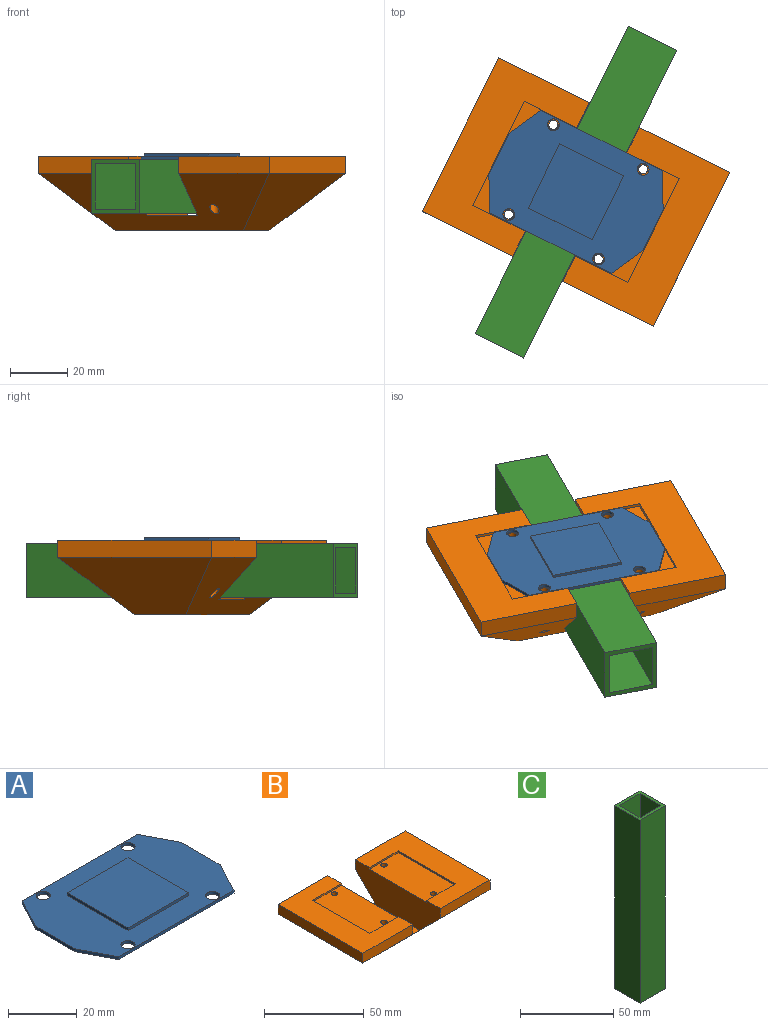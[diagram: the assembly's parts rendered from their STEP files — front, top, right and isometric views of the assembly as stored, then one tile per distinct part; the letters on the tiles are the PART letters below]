
ASSEMBLY  parts=3 mates=6
PART A: 19 faces, bbox 60x40x2 mm
  f0: plane 60x40mm, normal (0,0,1), area 1572.2mm2, adj f1,f2,f3,f4,f6,f7,f8,f9
  f1: plane 16x1mm, normal (1,0,0), area 16mm2, adj f0,f5,f12,f13
  f2: plane 47.5x1mm, normal (0,1,0), area 47.5mm2, adj f0,f5,f10,f13
  f3: plane 16x1mm, normal (-1,0,0), area 16mm2, adj f0,f5,f10,f11
  f4: plane 47.5x1mm, normal (0,-1,0), area 47.5mm2, adj f0,f5,f11,f12
  f5: plane 60x40mm, normal (0,0,-1), area 2197.2mm2, adj f1,f2,f3,f4,f6,f7,f8,f9
  f6: cylinder r=2.05mm len=4.1mm, axis (0,0,-1), area 12.9mm2, adj f0,f5
  f7: cylinder r=2.05mm len=4.1mm, axis (0,0,-1), area 12.9mm2, adj f0,f5
  f8: cylinder r=2.05mm len=4.1mm, axis (0,0,-1), area 12.9mm2, adj f0,f5
  f9: cylinder r=2.05mm len=4.1mm, axis (0,0,-1), area 12.9mm2, adj f0,f5
  f10: plane 12x6.25mm, normal (-0.89,0.46,0), area 13.5mm2, adj f0,f2,f3,f5
  f11: plane 12x6.25mm, normal (-0.89,-0.46,0), area 13.5mm2, adj f0,f3,f4,f5
  f12: plane 12x6.25mm, normal (0.89,-0.46,0), area 13.5mm2, adj f0,f1,f4,f5
  f13: plane 12x6.25mm, normal (0.89,0.46,0), area 13.5mm2, adj f0,f1,f2,f5
  f14: plane 25x1mm, normal (0,-1,0), area 25mm2, adj f0,f15,f17,f18
  f15: plane 25x1mm, normal (1,0,0), area 25mm2, adj f0,f14,f16,f18
  f16: plane 25x1mm, normal (0,1,0), area 25mm2, adj f0,f15,f17,f18
  f17: plane 25x1mm, normal (-1,0,0), area 25mm2, adj f0,f14,f16,f18
  f18: plane 25x25mm, normal (0,0,1), area 625mm2, adj f14,f15,f16,f17
PART B: 28 faces, bbox 90.7x60.7x26.7 mm
  f0: plane 35.23x6mm, normal (0,-1,0), area 211.4mm2, adj f7,f10,f12,f21
  f1: plane 35.23x6mm, normal (0,1,0), area 211.4mm2, adj f6,f9,f16,f22
  f2: plane 40.5x20.48mm, normal (0,0,1), area 813.2mm2, adj f10,f13,f14,f15,f24,f27
  f3: plane 40.5x20.48mm, normal (0,0,1), area 813.2mm2, adj f9,f17,f18,f19,f25,f26
  f4: plane 35.23x6mm, normal (0,-1,0), area 211.4mm2, adj f6,f9,f16,f21
  f5: plane 35.23x6mm, normal (0,1,0), area 211.4mm2, adj f7,f10,f12,f22
  f6: plane 60x6mm, normal (1,0,0), area 360mm2, adj f1,f4,f16,f20
  f7: plane 60x6mm, normal (-1,0,0), area 360mm2, adj f0,f5,f12,f23
  f8: plane 50x20mm, normal (0,0,-1), area 1000mm2, adj f20,f21,f22,f23
  f9: plane 60x20.55mm, normal (-1,0,0), area 980.8mm2, adj f1,f3,f4,f11,f16,f17,f18,f21
  f10: plane 60x20.55mm, normal (1,0,0), area 980.8mm2, adj f0,f2,f5,f11,f12,f13,f15,f21
  f11: plane 30.9x19.55mm, normal (0,0,1), area 604.1mm2, adj f9,f10,f21,f22
  f12: plane 60x35.23mm, normal (0,0,1), area 1284.3mm2, adj f0,f5,f7,f10,f13,f14,f15
  f13: plane 20.48x1mm, normal (0,1,0), area 20.5mm2, adj f2,f10,f12,f14
  f14: plane 40.5x1mm, normal (1,0,0), area 40.5mm2, adj f2,f12,f13,f15
  f15: plane 20.48x1mm, normal (0,-1,0), area 20.5mm2, adj f2,f10,f12,f14
  f16: plane 60x35.23mm, normal (0,0,1), area 1284.3mm2, adj f1,f4,f6,f9,f17,f18,f19
  f17: plane 20.48x1mm, normal (0,1,0), area 20.5mm2, adj f3,f9,f16,f19
  f18: plane 20.48x1mm, normal (0,-1,0), area 20.5mm2, adj f3,f9,f16,f19
  f19: plane 40.5x1mm, normal (-1,0,0), area 40.5mm2, adj f3,f16,f17,f18
  f20: plane 60x20mm, normal (0.71,0,-0.71), area 1131.4mm2, adj f6,f8,f21,f22
  f21: plane 90.67x20.67mm, normal (0,-0.71,-0.71), area 1554.9mm2, adj f0,f4,f8,f9,f10,f11,f20,f23
  f22: plane 90.67x20.67mm, normal (0,0.71,-0.71), area 1554.9mm2, adj f1,f5,f8,f9,f10,f11,f20,f23
  f23: plane 60x20mm, normal (-0.71,0,-0.71), area 1131.4mm2, adj f7,f8,f21,f22
  f24: cylinder r=1.6mm len=19.11mm, axis (0,0,1), area 176.5mm2, adj f2,f22
  f25: cylinder r=1.6mm len=19.11mm, axis (0,0,1), area 176.5mm2, adj f3,f22
  f26: cylinder r=1.6mm len=19.11mm, axis (0,0,1), area 176.5mm2, adj f3,f21
  f27: cylinder r=1.6mm len=19.11mm, axis (0,0,1), area 176.5mm2, adj f2,f21
PART C: 10 faces, bbox 19.1x19.1x120 mm
  f0: plane 120x19.05mm, normal (0,-1,0), area 2286mm2, adj f1,f7,f8,f9
  f1: plane 120x19.05mm, normal (1,0,0), area 2286mm2, adj f0,f2,f8,f9
  f2: plane 120x19.05mm, normal (0,1,0), area 2286mm2, adj f1,f7,f8,f9
  f3: plane 120x15.88mm, normal (0,-1,0), area 1905mm2, adj f4,f6,f8,f9
  f4: plane 120x15.88mm, normal (-1,0,0), area 1905mm2, adj f3,f5,f8,f9
  f5: plane 120x15.88mm, normal (0,1,0), area 1905mm2, adj f4,f6,f8,f9
  f6: plane 120x15.88mm, normal (1,0,0), area 1905mm2, adj f3,f5,f8,f9
  f7: plane 120x19.05mm, normal (-1,0,0), area 2286mm2, adj f0,f2,f8,f9
  f8: plane 19.05x19.05mm, normal (0,0,1), area 110.9mm2, adj f0,f1,f2,f3,f4,f5,f6,f7
  f9: plane 19.05x19.05mm, normal (0,0,-1), area 110.9mm2, adj f0,f1,f2,f3,f4,f5,f6,f7
PLACE A rot(axis=(0,0,1),153.6deg) t=(0,0,-1)mm
PLACE B rot(axis=(0,0,-1),26.4deg) t=(0,0,-1)mm
PLACE C rot(axis=(-0.47,0.75,0.47),106.1deg) t=(-26.72,-53.72,-10.52)mm
MATE cylindrical B.f24 <-> A.f6  axis (0,0,1) through (-7.88,23.46,-1)mm
MATE cylindrical C.f7 <-> A.f5  axis (0,0,1) through (0,0,-1)mm
MATE cylindrical B.f26 <-> A.f8  axis (0,0,1) through (7.88,-23.46,-1)mm
MATE planar C.f7 <-> A.f5  axis (0,0,1) through (0,0,-1)mm
MATE planar B.f3 <-> A.f5  axis (0,0,1) through (17.96,-8.93,-1)mm
MATE parallel C.f8 <-> A.f4  axis (0.45,0.9,0) through (26.72,53.72,-10.53)mm
